# Revit family: Shutter-Wood-Fypon-Board_Batten
name_source: partatom
category: Specialty Equipment
revit_build: Autodesk Revit 2017 (Build: 20160225_1515(x64)
units: mm (PartAtom-declared; Revit-internal decimal feet)

## family parameters
Cut with Voids When Loaded = No
Host = Face
OmniClass Number = 23.30.60.11.14
OmniClass Title = Exterior Shutters
Part Type = Normal
Room Calculation Point = No
Round Connector Dimension = Use Diameter
Shared = No

## types (144) — shared parameters
Assembly Code = B20
Board Depth = 0' - 1 1/2"
Default Elevation = 4' - 0"
Description = Rough Sawn Cedar Shutters
Finish = Wood-Fypon-Rough_Sawn
Manufacturer = Fypon
Product Documentation Link = http://www.fypon.com
Product Name = Board and Batten Shutter
Product Page URL = http://www.fypon.com
Specification = http://www.fypon.com
URL = http://www.fypon.com

## per-type parameters (varying)
| type | 2 Batten | 2 Board | 3 Batten | 3 Board | 3rd Board | 4 Board | Board Width | End Batten | End Batten Offset | Height | Model | Type Comments | Width | Z Batten |
| 2 Batten 12 x 24 | Yes | Yes | No | No | No | No | 0' - 6" | No | 0' - 5 19/32" | 2' - 0" | SH2PC12X24RS | 2 Board, 2 Batten | 1' - 0" | No |
| 2 Batten 12 x 36 | Yes | Yes | No | No | No | No | 0' - 6" | No | 0' - 5 19/32" | 3' - 0" | SH2PC12X36RS | 2 Board, 2 Batten | 1' - 0" | No |
| 2 Batten 12 x 48 | Yes | Yes | No | No | No | No | 0' - 6" | No | 0' - 5 19/32" | 4' - 0" | SH2PC12X48RS | 2 Board, 2 Batten | 1' - 0" | No |
| 2 Batten 12 x 60 | Yes | Yes | No | No | No | No | 0' - 6" | No | 0' - 5 19/32" | 5' - 0" | SH2PC12X60RS | 2 Board, 2 Batten | 1' - 0" | No |
| 2 Batten 12 x 72 | Yes | Yes | No | No | No | No | 0' - 6" | No | 0' - 5 19/32" | 6' - 0" | SH2PC12X72RS | 2 Board, 2 Batten | 1' - 0" | No |
| 2 Batten 12 x 84 | Yes | Yes | No | No | No | No | 0' - 6" | No | 0' - 5 19/32" | 7' - 0" | SH2PC12X84RS | 2 Board, 2 Batten | 1' - 0" | No |
| 2 Batten 12 x 96 | Yes | Yes | No | No | No | No | 0' - 6" | No | 0' - 5 19/32" | 8' - 0" | SH2PC12X96RS | 2 Board, 2 Batten | 1' - 0" | No |
| 2 Batten 12 x 108 | Yes | Yes | No | No | No | No | 0' - 6" | No | 0' - 5 19/32" | 9' - 0" | SH2PC12X108RS | 2 Board, 2 Batten | 1' - 0" | No |
| 2 Batten 12 x 120 | Yes | Yes | No | No | No | No | 0' - 6" | No | 0' - 5 19/32" | 10' - 0" | SH2PC12X120RS | 2 Board, 2 Batten | 1' - 0" | No |
| 3 Batten 12 x 24 | No | Yes | Yes | No | No | No | 0' - 6" | No | 0' - 5 19/32" | 2' - 0" | SH2P3BC12X24RS | 2 Board, 3 Batten | 1' - 0" | No |
| 3 Batten 12 x 36 | No | Yes | Yes | No | No | No | 0' - 6" | No | 0' - 5 19/32" | 3' - 0" | SH2P3BC12X36RS | 2 Board, 3 Batten | 1' - 0" | No |
| 3 Batten 12 x 48 | No | Yes | Yes | No | No | No | 0' - 6" | No | 0' - 5 19/32" | 4' - 0" | SH2P3BC12X48RS | 2 Board, 3 Batten | 1' - 0" | No |
| 3 Batten 12 x 60 | No | Yes | Yes | No | No | No | 0' - 6" | No | 0' - 5 19/32" | 5' - 0" | SH2P3BC12X60RS | 2 Board, 3 Batten | 1' - 0" | No |
| 3 Batten 12 x 72 | No | Yes | Yes | No | No | No | 0' - 6" | No | 0' - 5 19/32" | 6' - 0" | SH2P3BC12X72RS | 2 Board, 3 Batten | 1' - 0" | No |
| 3 Batten 12 x 84 | No | Yes | Yes | No | No | No | 0' - 6" | No | 0' - 5 19/32" | 7' - 0" | SH2P3BC12X84RS | 2 Board, 3 Batten | 1' - 0" | No |
| 3 Batten 12 x 96 | No | Yes | Yes | No | No | No | 0' - 6" | No | 0' - 5 19/32" | 8' - 0" | SH2P3BC12X96RS | 2 Board, 3 Batten | 1' - 0" | No |
| 3 Batten 12 x 108 | No | Yes | Yes | No | No | No | 0' - 6" | No | 0' - 5 19/32" | 9' - 0" | SH2P3BC12X108RS | 2 Board, 3 Batten | 1' - 0" | No |
| 3 Batten 12 x 120 | No | Yes | Yes | No | No | No | 0' - 6" | No | 0' - 5 19/32" | 10' - 0" | SH2P3BC12X120RS | 2 Board, 3 Batten | 1' - 0" | No |
| End Batten 12 x 24 | No | Yes | No | No | No | No | 0' - 6" | Yes | 0' - 0" | 2' - 0" | SH2PEBC12X24RS | 2 Board, End Batten | 1' - 0" | No |
| End Batten 12 x 36 | No | Yes | No | No | No | No | 0' - 6" | Yes | 0' - 0" | 3' - 0" | SH2PEBC12X36RS | 2 Board, End Batten | 1' - 0" | No |
| End Batten 12 x 48 | No | Yes | No | No | No | No | 0' - 6" | Yes | 0' - 0" | 4' - 0" | SH2PEBC12X48RS | 2 Board, End Batten | 1' - 0" | No |
| End Batten 12 x 60 | No | Yes | No | No | No | No | 0' - 6" | Yes | 0' - 0" | 5' - 0" | SH2PEBC12X60RS | 2 Board, End Batten | 1' - 0" | No |
| End Batten 12 x 72 | No | Yes | No | No | No | No | 0' - 6" | Yes | 0' - 0" | 6' - 0" | SH2PEBC12X72RS | 2 Board, End Batten | 1' - 0" | No |
| End Batten 12 x 84 | No | Yes | No | No | No | No | 0' - 6" | Yes | 0' - 0" | 7' - 0" | SH2PEBC12X84RS | 2 Board, End Batten | 1' - 0" | No |
| End Batten 12 x 96 | No | Yes | No | No | No | No | 0' - 6" | Yes | 0' - 0" | 8' - 0" | SH2PEBC12X96RS | 2 Board, End Batten | 1' - 0" | No |
| End Batten 12 x 108 | No | Yes | No | No | No | No | 0' - 6" | Yes | 0' - 0" | 9' - 0" | SH2PEBC12X108RS | 2 Board, End Batten | 1' - 0" | No |
| End Batten 12 x 120 | No | Yes | No | No | No | No | 0' - 6" | Yes | 0' - 0" | 10' - 0" | SH2PEBC12X120RS | 2 Board, End Batten | 1' - 0" | No |
| Z Batten 12 x 24 | Yes | Yes | No | No | No | No | 0' - 6" | No | 0' - 5 19/32" | 2' - 0" | SH2PZC12X24RS | 2 Board, Z Batten | 1' - 0" | Yes |
| Z Batten 12 x 36 | Yes | Yes | No | No | No | No | 0' - 6" | No | 0' - 5 19/32" | 3' - 0" | SH2PZC12X36RS | 2 Board, Z Batten | 1' - 0" | Yes |
| Z Batten 12 x 48 | Yes | Yes | No | No | No | No | 0' - 6" | No | 0' - 5 19/32" | 4' - 0" | SH2PZC12X48RS | 2 Board, Z Batten | 1' - 0" | Yes |
| Z Batten 12 x 60 | Yes | Yes | No | No | No | No | 0' - 6" | No | 0' - 5 19/32" | 5' - 0" | SH2PZC12X60RS | 2 Board, Z Batten | 1' - 0" | Yes |
| Z Batten 12 x 72 | Yes | Yes | No | No | No | No | 0' - 6" | No | 0' - 5 19/32" | 6' - 0" | SH2PZC12X72RS | 2 Board, Z Batten | 1' - 0" | Yes |
| Z Batten 12 x 84 | Yes | Yes | No | No | No | No | 0' - 6" | No | 0' - 5 19/32" | 7' - 0" | SH2PZC12X84RS | 2 Board, Z Batten | 1' - 0" | Yes |
| Z Batten 12 x 96 | Yes | Yes | No | No | No | No | 0' - 6" | No | 0' - 5 19/32" | 8' - 0" | SH2PZC12X96RS | 2 Board, Z Batten | 1' - 0" | Yes |
| Z Batten 12 x 108 | Yes | Yes | No | No | No | No | 0' - 6" | No | 0' - 5 19/32" | 9' - 0" | SH2PZC12X108RS | 2 Board, Z Batten | 1' - 0" | Yes |
| Z Batten 12 x 120 | Yes | Yes | No | No | No | No | 0' - 6" | No | 0' - 5 19/32" | 10' - 0" | SH2PZC12X120RS | 2 Board, Z Batten | 1' - 0" | Yes |
| 2 Batten 14 x 24 | Yes | No | No | Yes | Yes | No | 0' - 4 21/32" | No | 0' - 5 19/32" | 2' - 0" | SH3PC14X24RS | 3 Board, 2 Batten | 1' - 2" | No |
| 2 Batten 14 x 36 | Yes | No | No | Yes | Yes | No | 0' - 4 21/32" | No | 0' - 5 19/32" | 3' - 0" | SH3PC14X36RS | 3 Board, 2 Batten | 1' - 2" | No |
| 2 Batten 14 x 48 | Yes | No | No | Yes | Yes | No | 0' - 4 21/32" | No | 0' - 5 19/32" | 4' - 0" | SH3PC14X48RS | 3 Board, 2 Batten | 1' - 2" | No |
| 2 Batten 14 x 60 | Yes | No | No | Yes | Yes | No | 0' - 4 21/32" | No | 0' - 5 19/32" | 5' - 0" | SH3PC14X60RS | 3 Board, 2 Batten | 1' - 2" | No |
| 2 Batten 14 x 72 | Yes | No | No | Yes | Yes | No | 0' - 4 21/32" | No | 0' - 5 19/32" | 6' - 0" | SH3PC14X72RS | 3 Board, 2 Batten | 1' - 2" | No |
| 2 Batten 14 x 84 | Yes | No | No | Yes | Yes | No | 0' - 4 21/32" | No | 0' - 5 19/32" | 7' - 0" | SH3PC14X84RS | 3 Board, 2 Batten | 1' - 2" | No |
| 2 Batten 14 x 96 | Yes | No | No | Yes | Yes | No | 0' - 4 21/32" | No | 0' - 5 19/32" | 8' - 0" | SH3PC14X96RS | 3 Board, 2 Batten | 1' - 2" | No |
| 2 Batten 14 x 108 | Yes | No | No | Yes | Yes | No | 0' - 4 21/32" | No | 0' - 5 19/32" | 9' - 0" | SH3PC14X108RS | 3 Board, 2 Batten | 1' - 2" | No |
| 2 Batten 14 x 120 | Yes | No | No | Yes | Yes | No | 0' - 4 21/32" | No | 0' - 5 19/32" | 10' - 0" | SH3PC14X120RS | 3 Board, 2 Batten | 1' - 2" | No |
| 3 Batten 14 x 24 | No | No | Yes | Yes | Yes | No | 0' - 4 21/32" | No | 0' - 5 19/32" | 2' - 0" | SH3P3BC14X24RS | 3 Board, 3 Batten | 1' - 2" | No |
| 3 Batten 14 x 36 | No | No | Yes | Yes | Yes | No | 0' - 4 21/32" | No | 0' - 5 19/32" | 3' - 0" | SH3P3BC14X36RS | 3 Board, 3 Batten | 1' - 2" | No |
| 3 Batten 14 x 48 | No | No | Yes | Yes | Yes | No | 0' - 4 21/32" | No | 0' - 5 19/32" | 4' - 0" | SH3P3BC14X48RS | 3 Board, 3 Batten | 1' - 2" | No |
| 3 Batten 14 x 60 | No | No | Yes | Yes | Yes | No | 0' - 4 21/32" | No | 0' - 5 19/32" | 5' - 0" | SH3P3BC14X60RS | 3 Board, 3 Batten | 1' - 2" | No |
| 3 Batten 14 x 72 | No | No | Yes | Yes | Yes | No | 0' - 4 21/32" | No | 0' - 5 19/32" | 6' - 0" | SH3P3BC14X72RS | 3 Board, 3 Batten | 1' - 2" | No |
| 3 Batten 14 x 84 | No | No | Yes | Yes | Yes | No | 0' - 4 21/32" | No | 0' - 5 19/32" | 7' - 0" | SH3P3BC14X84RS | 3 Board, 3 Batten | 1' - 2" | No |
| 3 Batten 14 x 96 | No | No | Yes | Yes | Yes | No | 0' - 4 21/32" | No | 0' - 5 19/32" | 8' - 0" | SH3P3BC14X96RS | 3 Board, 3 Batten | 1' - 2" | No |
| 3 Batten 14 x 108 | No | No | Yes | Yes | Yes | No | 0' - 4 21/32" | No | 0' - 5 19/32" | 9' - 0" | SH3P3BC14X108RS | 3 Board, 3 Batten | 1' - 2" | No |
| 3 Batten 14 x 120 | No | No | Yes | Yes | Yes | No | 0' - 4 21/32" | No | 0' - 5 19/32" | 10' - 0" | SH3P3BC14X120RS | 3 Board, 3 Batten | 1' - 2" | No |
| End Batten 14 x 24 | No | No | No | Yes | Yes | No | 0' - 4 21/32" | Yes | 0' - 0" | 2' - 0" | SH3PEBC14X24RS | 3 Board, End Batten | 1' - 2" | No |
| End Batten 14 x 36 | No | No | No | Yes | Yes | No | 0' - 4 21/32" | Yes | 0' - 0" | 3' - 0" | SH3PEBC14X36RS | 3 Board, End Batten | 1' - 2" | No |
| End Batten 14 x 48 | No | No | No | Yes | Yes | No | 0' - 4 21/32" | Yes | 0' - 0" | 4' - 0" | SH3PEBC14X48RS | 3 Board, End Batten | 1' - 2" | No |
| End Batten 14 x 60 | No | No | No | Yes | Yes | No | 0' - 4 21/32" | Yes | 0' - 0" | 5' - 0" | SH3PEBC14X60RS | 3 Board, End Batten | 1' - 2" | No |
| End Batten 14 x 72 | No | No | No | Yes | Yes | No | 0' - 4 21/32" | Yes | 0' - 0" | 6' - 0" | SH3PEBC14X72RS | 3 Board, End Batten | 1' - 2" | No |
| End Batten 14 x 84 | No | No | No | Yes | Yes | No | 0' - 4 21/32" | Yes | 0' - 0" | 7' - 0" | SH3PEBC14X84RS | 3 Board, End Batten | 1' - 2" | No |
| End Batten 14 x 96 | No | No | No | Yes | Yes | No | 0' - 4 21/32" | Yes | 0' - 0" | 8' - 0" | SH3PEBC14X96RS | 3 Board, End Batten | 1' - 2" | No |
| End Batten 14 x 108 | No | No | No | Yes | Yes | No | 0' - 4 21/32" | Yes | 0' - 0" | 9' - 0" | SH3PEBC14X108RS | 3 Board, End Batten | 1' - 2" | No |
| End Batten 14 x 120 | No | No | No | Yes | Yes | No | 0' - 4 21/32" | Yes | 0' - 0" | 10' - 0" | SH3PEBC14X120RS | 3 Board, End Batten | 1' - 2" | No |
| Z Batten 14 x 24 | Yes | No | No | Yes | Yes | No | 0' - 4 21/32" | No | 0' - 5 19/32" | 2' - 0" | SH3PZC14X24RS | 3 Board, Z Batten | 1' - 2" | Yes |
| Z Batten 14 x 36 | Yes | No | No | Yes | Yes | No | 0' - 4 21/32" | No | 0' - 5 19/32" | 3' - 0" | SH3PZC14X36RS | 3 Board, Z Batten | 1' - 2" | Yes |
| Z Batten 14 x 48 | Yes | No | No | Yes | Yes | No | 0' - 4 21/32" | No | 0' - 5 19/32" | 4' - 0" | SH3PZC14X48RS | 3 Board, Z Batten | 1' - 2" | Yes |
| Z Batten 14 x 60 | Yes | No | No | Yes | Yes | No | 0' - 4 21/32" | No | 0' - 5 19/32" | 5' - 0" | SH3PZC14X60RS | 3 Board, Z Batten | 1' - 2" | Yes |
| Z Batten 14 x 72 | Yes | No | No | Yes | Yes | No | 0' - 4 21/32" | No | 0' - 5 19/32" | 6' - 0" | SH3PZC14X72RS | 3 Board, Z Batten | 1' - 2" | Yes |
| Z Batten 14 x 84 | Yes | No | No | Yes | Yes | No | 0' - 4 21/32" | No | 0' - 5 19/32" | 7' - 0" | SH3PZC14X84RS | 3 Board, Z Batten | 1' - 2" | Yes |
| Z Batten 14 x 96 | Yes | No | No | Yes | Yes | No | 0' - 4 21/32" | No | 0' - 5 19/32" | 8' - 0" | SH3PZC14X96RS | 3 Board, Z Batten | 1' - 2" | Yes |
| Z Batten 14 x 108 | Yes | No | No | Yes | Yes | No | 0' - 4 21/32" | No | 0' - 5 19/32" | 9' - 0" | SH3PZC14X108RS | 3 Board, Z Batten | 1' - 2" | Yes |
| Z Batten 14 x 120 | Yes | No | No | Yes | Yes | No | 0' - 4 21/32" | No | 0' - 5 19/32" | 10' - 0" | SH3PZC14X120RS | 3 Board, Z Batten | 1' - 2" | Yes |
| 2 Batten 18 x 24 | Yes | No | No | Yes | Yes | No | 0' - 6" | No | 0' - 5 19/32" | 2' - 0" | SH3PC18X24RS | 3 Board, 2 Batten | 1' - 6" | No |
| 2 Batten 18 x 36 | Yes | No | No | Yes | Yes | No | 0' - 6" | No | 0' - 5 19/32" | 3' - 0" | SH3PC18X36RS | 3 Board, 2 Batten | 1' - 6" | No |
| 2 Batten 18 x 48 | Yes | No | No | Yes | Yes | No | 0' - 6" | No | 0' - 5 19/32" | 4' - 0" | SH3PC18X48RS | 3 Board, 2 Batten | 1' - 6" | No |
| 2 Batten 18 x 60 | Yes | No | No | Yes | Yes | No | 0' - 6" | No | 0' - 5 19/32" | 5' - 0" | SH3PC18X60RS | 3 Board, 2 Batten | 1' - 6" | No |
| 2 Batten 18 x 72 | Yes | No | No | Yes | Yes | No | 0' - 6" | No | 0' - 5 19/32" | 6' - 0" | SH3PC18X72RS | 3 Board, 2 Batten | 1' - 6" | No |
| 2 Batten 18 x 84 | Yes | No | No | Yes | Yes | No | 0' - 6" | No | 0' - 5 19/32" | 7' - 0" | SH3PC18X84RS | 3 Board, 2 Batten | 1' - 6" | No |
| 2 Batten 18 x 96 | Yes | No | No | Yes | Yes | No | 0' - 6" | No | 0' - 5 19/32" | 8' - 0" | SH3PC18X96RS | 3 Board, 2 Batten | 1' - 6" | No |
| 2 Batten 18 x 108 | Yes | No | No | Yes | Yes | No | 0' - 6" | No | 0' - 5 19/32" | 9' - 0" | SH3PC18X108RS | 3 Board, 2 Batten | 1' - 6" | No |
| 2 Batten 18 x 120 | Yes | No | No | Yes | Yes | No | 0' - 6" | No | 0' - 5 19/32" | 10' - 0" | SH3PC18X120RS | 3 Board, 2 Batten | 1' - 6" | No |
| 3 Batten 18 x 24 | No | No | Yes | Yes | Yes | No | 0' - 6" | No | 0' - 5 19/32" | 2' - 0" | SH3P3BC18X24RS | 3 Board, 3 Batten | 1' - 6" | No |
| 3 Batten 18 x 36 | No | No | Yes | Yes | Yes | No | 0' - 6" | No | 0' - 5 19/32" | 3' - 0" | SH3P3BC18X36RS | 3 Board, 3 Batten | 1' - 6" | No |
| 3 Batten 18 x 48 | No | No | Yes | Yes | Yes | No | 0' - 6" | No | 0' - 5 19/32" | 4' - 0" | SH3P3BC18X48RS | 3 Board, 3 Batten | 1' - 6" | No |
| 3 Batten 18 x 60 | No | No | Yes | Yes | Yes | No | 0' - 6" | No | 0' - 5 19/32" | 5' - 0" | SH3P3BC18X60RS | 3 Board, 3 Batten | 1' - 6" | No |
| 3 Batten 18 x 72 | No | No | Yes | Yes | Yes | No | 0' - 6" | No | 0' - 5 19/32" | 6' - 0" | SH3P3BC18X72RS | 3 Board, 3 Batten | 1' - 6" | No |
| 3 Batten 18 x 84 | No | No | Yes | Yes | Yes | No | 0' - 6" | No | 0' - 5 19/32" | 7' - 0" | SH3P3BC18X84RS | 3 Board, 3 Batten | 1' - 6" | No |
| 3 Batten 18 x 96 | No | No | Yes | Yes | Yes | No | 0' - 6" | No | 0' - 5 19/32" | 8' - 0" | SH3P3BC18X96RS | 3 Board, 3 Batten | 1' - 6" | No |
| 3 Batten 18 x 108 | No | No | Yes | Yes | Yes | No | 0' - 6" | No | 0' - 5 19/32" | 9' - 0" | SH3P3BC18X108RS | 3 Board, 3 Batten | 1' - 6" | No |
| 3 Batten 18 x 120 | No | No | Yes | Yes | Yes | No | 0' - 6" | No | 0' - 5 19/32" | 10' - 0" | SH3P3BC18X120RS | 3 Board, 3 Batten | 1' - 6" | No |
| End Batten 18 x 24 | No | No | No | Yes | Yes | No | 0' - 6" | Yes | 0' - 0" | 2' - 0" | SH3PEBC18X24RS | 3 Board, End Batten | 1' - 6" | No |
| End Batten 18 x 36 | No | No | No | Yes | Yes | No | 0' - 6" | Yes | 0' - 0" | 3' - 0" | SH3PEBC18X36RS | 3 Board, End Batten | 1' - 6" | No |
| End Batten 18 x 48 | No | No | No | Yes | Yes | No | 0' - 6" | Yes | 0' - 0" | 4' - 0" | SH3PEBC18X48RS | 3 Board, End Batten | 1' - 6" | No |
| End Batten 18 x 60 | No | No | No | Yes | Yes | No | 0' - 6" | Yes | 0' - 0" | 5' - 0" | SH3PEBC18X60RS | 3 Board, End Batten | 1' - 6" | No |
| End Batten 18 x 72 | No | No | No | Yes | Yes | No | 0' - 6" | Yes | 0' - 0" | 6' - 0" | SH3PEBC18X72RS | 3 Board, End Batten | 1' - 6" | No |
| End Batten 18 x 84 | No | No | No | Yes | Yes | No | 0' - 6" | Yes | 0' - 0" | 7' - 0" | SH3PEBC18X84RS | 3 Board, End Batten | 1' - 6" | No |
| End Batten 18 x 96 | No | No | No | Yes | Yes | No | 0' - 6" | Yes | 0' - 0" | 8' - 0" | SH3PEBC18X96RS | 3 Board, End Batten | 1' - 6" | No |
| End Batten 18 x 108 | No | No | No | Yes | Yes | No | 0' - 6" | Yes | 0' - 0" | 9' - 0" | SH3PEBC18X108RS | 3 Board, End Batten | 1' - 6" | No |
| End Batten 18 x 120 | No | No | No | Yes | Yes | No | 0' - 6" | Yes | 0' - 0" | 10' - 0" | SH3PEBC18X120RS | 3 Board, End Batten | 1' - 6" | No |
| Z Batten 18 x 24 | Yes | No | No | Yes | Yes | No | 0' - 6" | No | 0' - 5 19/32" | 2' - 0" | SH3PZC18X24RS | 3 Board, Z Batten | 1' - 6" | Yes |
| Z Batten 18 x 36 | Yes | No | No | Yes | Yes | No | 0' - 6" | No | 0' - 5 19/32" | 3' - 0" | SH3PZC18X36RS | 3 Board, Z Batten | 1' - 6" | Yes |
| Z Batten 18 x 48 | Yes | No | No | Yes | Yes | No | 0' - 6" | No | 0' - 5 19/32" | 4' - 0" | SH3PZC18X48RS | 3 Board, Z Batten | 1' - 6" | Yes |
| Z Batten 18 x 60 | Yes | No | No | Yes | Yes | No | 0' - 6" | No | 0' - 5 19/32" | 5' - 0" | SH3PZC18X60RS | 3 Board, Z Batten | 1' - 6" | Yes |
| Z Batten 18 x 72 | Yes | No | No | Yes | Yes | No | 0' - 6" | No | 0' - 5 19/32" | 6' - 0" | SH3PZC18X72RS | 3 Board, Z Batten | 1' - 6" | Yes |
| Z Batten 18 x 84 | Yes | No | No | Yes | Yes | No | 0' - 6" | No | 0' - 5 19/32" | 7' - 0" | SH3PZC18X84RS | 3 Board, Z Batten | 1' - 6" | Yes |
| Z Batten 18 x 96 | Yes | No | No | Yes | Yes | No | 0' - 6" | No | 0' - 5 19/32" | 8' - 0" | SH3PZC18X96RS | 3 Board, Z Batten | 1' - 6" | Yes |
| Z Batten 18 x 108 | Yes | No | No | Yes | Yes | No | 0' - 6" | No | 0' - 5 19/32" | 9' - 0" | SH3PZC18X108RS | 3 Board, Z Batten | 1' - 6" | Yes |
| Z Batten 18 x 120 | Yes | No | No | Yes | Yes | No | 0' - 6" | No | 0' - 5 19/32" | 10' - 0" | SH3PZC18X120RS | 3 Board, Z Batten | 1' - 6" | Yes |
| 2 Batten 24 x 24 | Yes | No | No | No | Yes | Yes | 0' - 6" | No | 0' - 5 19/32" | 2' - 0" | SH4PC24X24RS | 4 Board, 2 Batten | 2' - 0" | No |
| 2 Batten 24 x 36 | Yes | No | No | No | Yes | Yes | 0' - 6" | No | 0' - 5 19/32" | 3' - 0" | SH4PC24X36RS | 4 Board, 2 Batten | 2' - 0" | No |
| 2 Batten 24 x 48 | Yes | No | No | No | Yes | Yes | 0' - 6" | No | 0' - 5 19/32" | 4' - 0" | SH4PC24X48RS | 4 Board, 2 Batten | 2' - 0" | No |
| 2 Batten 24 x 60 | Yes | No | No | No | Yes | Yes | 0' - 6" | No | 0' - 5 19/32" | 5' - 0" | SH4PC24X60RS | 4 Board, 2 Batten | 2' - 0" | No |
| 2 Batten 24 x 72 | Yes | No | No | No | Yes | Yes | 0' - 6" | No | 0' - 5 19/32" | 6' - 0" | SH4PC24X72RS | 4 Board, 2 Batten | 2' - 0" | No |
| 2 Batten 24 x 84 | Yes | No | No | No | Yes | Yes | 0' - 6" | No | 0' - 5 19/32" | 7' - 0" | SH4PC24X84RS | 4 Board, 2 Batten | 2' - 0" | No |
| 2 Batten 24 x 96 | Yes | No | No | No | Yes | Yes | 0' - 6" | No | 0' - 5 19/32" | 8' - 0" | SH4PC24X96RS | 4 Board, 2 Batten | 2' - 0" | No |
| 2 Batten 24 x 108 | Yes | No | No | No | Yes | Yes | 0' - 6" | No | 0' - 5 19/32" | 9' - 0" | SH4PC24X108RS | 4 Board, 2 Batten | 2' - 0" | No |
| 2 Batten 24 x 120 | Yes | No | No | No | Yes | Yes | 0' - 6" | No | 0' - 5 19/32" | 10' - 0" | SH4PC24X120RS | 4 Board, 2 Batten | 2' - 0" | No |
| 3 Batten 24 x 24 | No | No | Yes | No | Yes | Yes | 0' - 6" | No | 0' - 5 19/32" | 2' - 0" | SH4P4BC24X24RS | 4 Board, 3 Batten | 2' - 0" | No |
| 3 Batten 24 x 36 | No | No | Yes | No | Yes | Yes | 0' - 6" | No | 0' - 5 19/32" | 3' - 0" | SH4P4BC24X36RS | 4 Board, 3 Batten | 2' - 0" | No |
| 3 Batten 24 x 48 | No | No | Yes | No | Yes | Yes | 0' - 6" | No | 0' - 5 19/32" | 4' - 0" | SH4P4BC24X48RS | 4 Board, 3 Batten | 2' - 0" | No |
| 3 Batten 24 x 60 | No | No | Yes | No | Yes | Yes | 0' - 6" | No | 0' - 5 19/32" | 5' - 0" | SH4P4BC24X60RS | 4 Board, 3 Batten | 2' - 0" | No |
| 3 Batten 24 x 72 | No | No | Yes | No | Yes | Yes | 0' - 6" | No | 0' - 5 19/32" | 6' - 0" | SH4P4BC24X72RS | 4 Board, 3 Batten | 2' - 0" | No |
| 3 Batten 24 x 84 | No | No | Yes | No | Yes | Yes | 0' - 6" | No | 0' - 5 19/32" | 7' - 0" | SH4P4BC24X84RS | 4 Board, 3 Batten | 2' - 0" | No |
| 3 Batten 24 x 96 | No | No | Yes | No | Yes | Yes | 0' - 6" | No | 0' - 5 19/32" | 8' - 0" | SH4P4BC24X96RS | 4 Board, 3 Batten | 2' - 0" | No |
| 3 Batten 24 x 108 | No | No | Yes | No | Yes | Yes | 0' - 6" | No | 0' - 5 19/32" | 9' - 0" | SH4P4BC24X108RS | 4 Board, 3 Batten | 2' - 0" | No |
| 3 Batten 24 x 120 | No | No | Yes | No | Yes | Yes | 0' - 6" | No | 0' - 5 19/32" | 10' - 0" | SH4P4BC24X120RS | 4 Board, 3 Batten | 2' - 0" | No |
| End Batten 24 x 24 | No | No | No | No | Yes | Yes | 0' - 6" | Yes | 0' - 0" | 2' - 0" | SH4PEBC24X24RS | 4 Board, End Batten | 2' - 0" | No |
| End Batten 24 x 36 | No | No | No | No | Yes | Yes | 0' - 6" | Yes | 0' - 0" | 3' - 0" | SH4PEBC24X36RS | 4 Board, End Batten | 2' - 0" | No |
| End Batten 24 x 48 | No | No | No | No | Yes | Yes | 0' - 6" | Yes | 0' - 0" | 4' - 0" | SH4PEBC24X48RS | 4 Board, End Batten | 2' - 0" | No |
| End Batten 24 x 60 | No | No | No | No | Yes | Yes | 0' - 6" | Yes | 0' - 0" | 5' - 0" | SH4PEBC24X60RS | 4 Board, End Batten | 2' - 0" | No |
| End Batten 24 x 72 | No | No | No | No | Yes | Yes | 0' - 6" | Yes | 0' - 0" | 6' - 0" | SH4PEBC24X72RS | 4 Board, End Batten | 2' - 0" | No |
| End Batten 24 x 84 | No | No | No | No | Yes | Yes | 0' - 6" | Yes | 0' - 0" | 7' - 0" | SH4PEBC24X84RS | 4 Board, End Batten | 2' - 0" | No |
| End Batten 24 x 96 | No | No | No | No | Yes | Yes | 0' - 6" | Yes | 0' - 0" | 8' - 0" | SH4PEBC24X96RS | 4 Board, End Batten | 2' - 0" | No |
| End Batten 24 x 108 | No | No | No | No | Yes | Yes | 0' - 6" | Yes | 0' - 0" | 9' - 0" | SH4PEBC24X108RS | 4 Board, End Batten | 2' - 0" | No |
| End Batten 24 x 120 | No | No | No | No | Yes | Yes | 0' - 6" | Yes | 0' - 0" | 10' - 0" | SH4PEBC24X120RS | 4 Board, End Batten | 2' - 0" | No |
| Z Batten 24 x 24 | Yes | No | No | No | Yes | Yes | 0' - 6" | No | 0' - 5 19/32" | 2' - 0" | SH4PZC24X24RS | 4 Board, Z Batten | 2' - 0" | Yes |
| Z Batten 24 x 36 | Yes | No | No | No | Yes | Yes | 0' - 6" | No | 0' - 5 19/32" | 3' - 0" | SH4PZC24X36RS | 4 Board, Z Batten | 2' - 0" | Yes |
| Z Batten 24 x 48 | Yes | No | No | No | Yes | Yes | 0' - 6" | No | 0' - 5 19/32" | 4' - 0" | SH4PZC24X48RS | 4 Board, Z Batten | 2' - 0" | Yes |
| Z Batten 24 x 60 | Yes | No | No | No | Yes | Yes | 0' - 6" | No | 0' - 5 19/32" | 5' - 0" | SH4PZC24X60RS | 4 Board, Z Batten | 2' - 0" | Yes |
| Z Batten 24 x 72 | Yes | No | No | No | Yes | Yes | 0' - 6" | No | 0' - 5 19/32" | 6' - 0" | SH4PZC24X72RS | 4 Board, Z Batten | 2' - 0" | Yes |
| Z Batten 24 x 84 | Yes | No | No | No | Yes | Yes | 0' - 6" | No | 0' - 5 19/32" | 7' - 0" | SH4PZC24X84RS | 4 Board, Z Batten | 2' - 0" | Yes |
| Z Batten 24 x 96 | Yes | No | No | No | Yes | Yes | 0' - 6" | No | 0' - 5 19/32" | 8' - 0" | SH4PZC24X96RS | 4 Board, Z Batten | 2' - 0" | Yes |
| Z Batten 24 x 108 | Yes | No | No | No | Yes | Yes | 0' - 6" | No | 0' - 5 19/32" | 9' - 0" | SH4PZC24X108RS | 4 Board, Z Batten | 2' - 0" | Yes |
| Z Batten 24 x 120 | Yes | No | No | No | Yes | Yes | 0' - 6" | No | 0' - 5 19/32" | 10' - 0" | SH4PZC24X120RS | 4 Board, Z Batten | 2' - 0" | Yes |

## geometry (parser evidence)
native form markers: Blend x4, Sweep x2
no freeform markers — native parametric forms only
